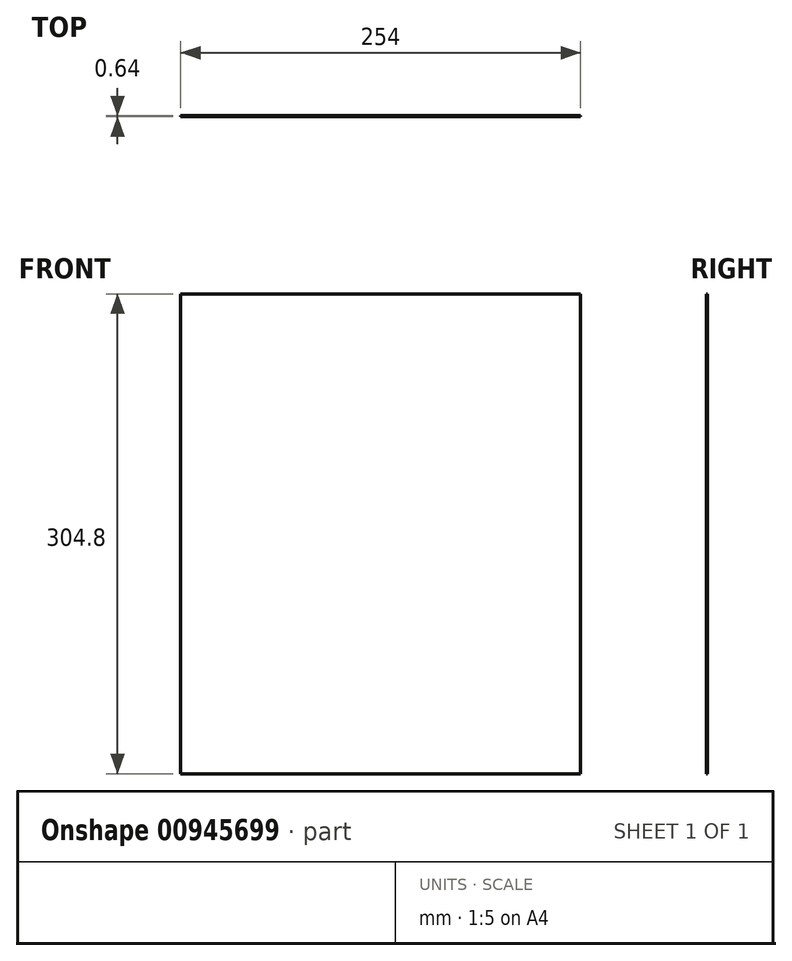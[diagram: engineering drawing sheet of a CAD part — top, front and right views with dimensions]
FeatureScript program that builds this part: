
annotation { "Feature Type Name" : "Feature", "Feature Type Description" : "" }
export const myFeature = defineFeature(function(context is Context, id is Id, definition is map)
    precondition{}
    {
        {
            var Q0;
            Q0=qCreatedBy(makeId("Front.planeOp"),FACE);
            var sketch = newSketch(context, id + "F0", { "sketchPlane" : qUnion([Q0])});
            skLineSegment(sketch, "E0", {"start": v(0, 304.8) * mm, "end": v(254, 304.8) * mm});
            skLineSegment(sketch, "E1", {"start": v(0, 304.8) * mm, "end": v(0, 0) * mm});
            skLineSegment(sketch, "E2", {"start": v(0, 0) * mm, "end": v(254, 0) * mm});
            skLineSegment(sketch, "E3", {"start": v(254, 304.8) * mm, "end": v(254, 0) * mm});
            skSolve(sketch);
        }
        {
            var Q0;
            Q0=makeQuery(id+"F0.imprint","IMPRINT",FACE,{"disambiguationData":[TD([[makeQuery(id+"F0.imprint","IMPRINT",EDGE,{"derivedFrom":sQuery(id+"F0.wireOp",EDGE,"E0")}),-1.0]])]});
            extrude(context, id + "F1", {"entities" : qUnion([Q0]), "depth" : 0.64 * mm, "offsetDistance" : 25.4 * mm});
        }
    });
